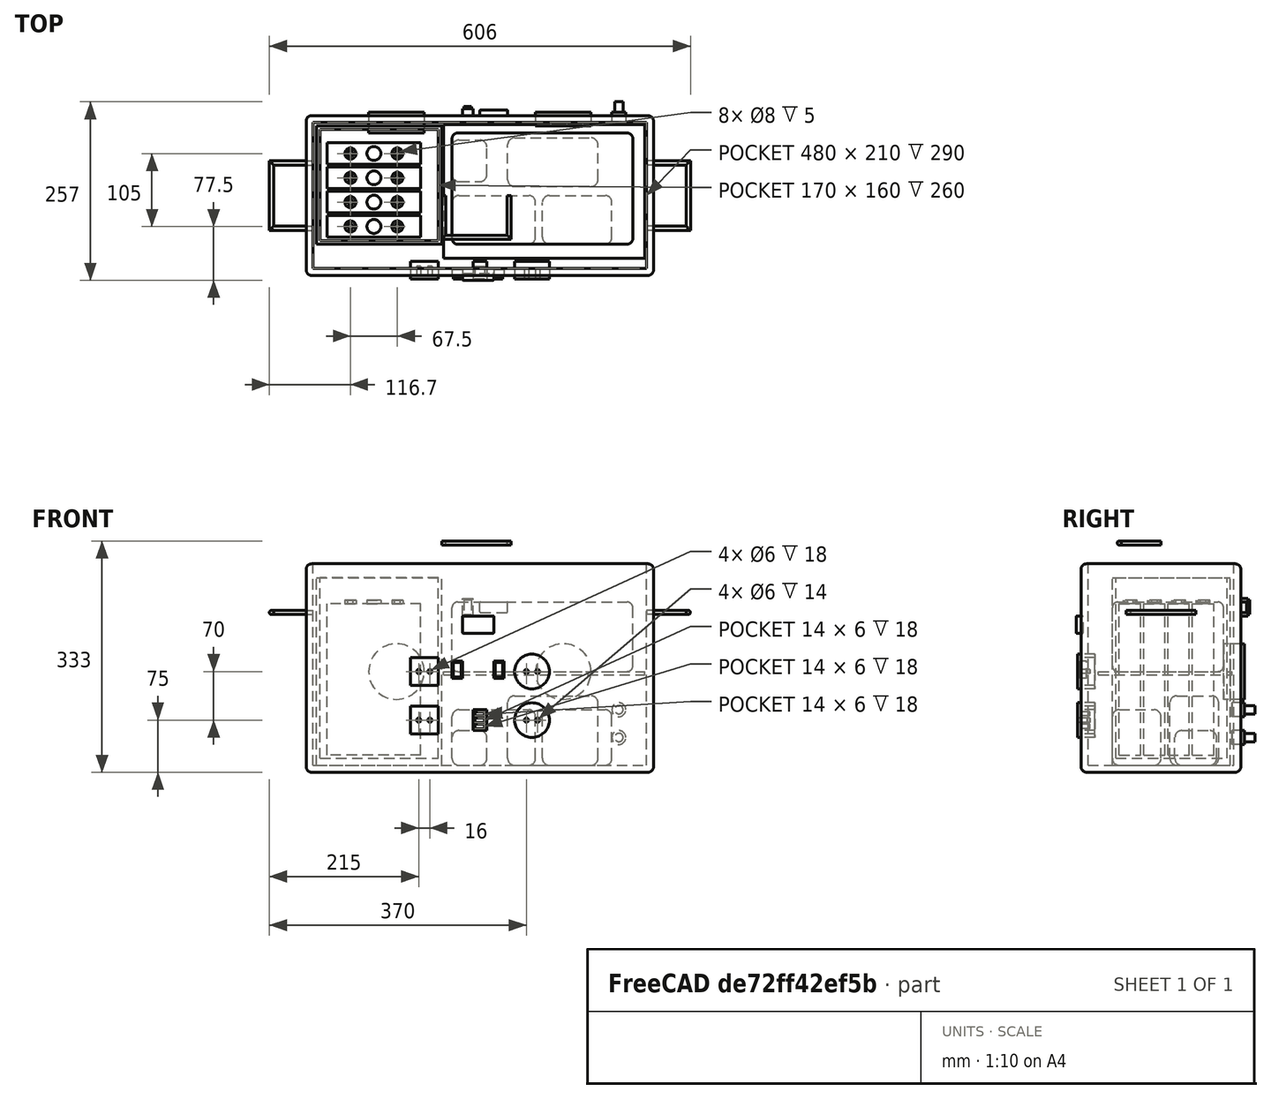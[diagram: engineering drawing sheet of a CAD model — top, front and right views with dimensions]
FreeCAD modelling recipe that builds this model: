
FCSTD DOCUMENT  (FreeCAD 0.16R6706 (Git))
Label: HOOU_FreeCAD_Solar_Box_v_02
License: All rights reserved
LicenseURL: http://en.wikipedia.org/wiki/All_rights_reserved
objects: Part::Box×26, Part::Cylinder×25, Part::Cut×14, Part::Fuse×11, Part::Fillet×9, Sketcher::SketchObject×4, PartDesign::Body×4, PartDesign::Pad×2, App::DocumentObjectGroup×1
note: 97 computed .brp shape members not serialized (recipe doc carries the construction recipe); baked Part::Feature solids carry a one-line shape summary decoded from their .brp

FEATURE [Part::Box] Box  label="Cube"
  Height = 300
  Length = 500
  Width = 230
FEATURE [Part::Box] Box001  label="Cube001"
  Height = 320
  Length = 480
  Placement = pos=(10,10,10) rot=(0,0,1;0rad)
  Width = 210
FEATURE [Part::Cut] Cut  label="Solar Box"
  Base = -> Box
  Tool = -> Box001
FEATURE [Sketcher::SketchObject] Sketch
FEATURE [Part::Box] Box002  label="Akku_box"
  Height = 290
  Length = 170
  Placement = pos=(20,50,20) rot=(0,0,1;0rad)
  Width = 160
FEATURE [Part::Box] Box003  label="MPPT"
  Height = 100
  Length = 130
  Placement = pos=(290,128,10) rot=(0,0,1;0rad)
  Width = 70
FEATURE [Part::Cylinder] Cylinder001  label="Fan 1"
  Angle = 360
  Height = 20
  Placement = pos=(370,235,145) rot=(1,0,0;1.5708rad)
  Radius = 40
FEATURE [PartDesign::Body] Body  label="AKKU 001"
  Placement = pos=(165,55,25) rot=(0,0,1;1.5708rad)
FEATURE [Sketcher::SketchObject] Sketch001
  sketch-geometry (4):
    g0: LineSegment StartX=0 StartY=135.1 StartZ=0 EndX=31 EndY=135.1 EndZ=0
    g1: LineSegment StartX=31 StartY=135.1 StartZ=0 EndX=31 EndY=0 EndZ=0
    g2: LineSegment StartX=31 StartY=0 StartZ=0 EndX=0 EndY=0 EndZ=0
    g3: LineSegment StartX=0 StartY=0 StartZ=0 EndX=0 EndY=135.1 EndZ=0
  constraints (11):
    c: Coincident(g0,g1)
    c: Coincident(g1,g2)
    c: Coincident(g2,g3)
    c: Coincident(g3,g0)
    c: Horizontal(g0)
    c: Horizontal(g2)
    c: Vertical(g1)
    c: Vertical(g3)
    c: Coincident(g2,g-1)
    c: DistanceY(g3,g3) = 135.1
    c: DistanceX(g2,g2) = 31
FEATURE [PartDesign::Pad] Pad
  Length = 217.3
  Length2 = 100
  Type = 0
FEATURE [Sketcher::SketchObject] Sketch002
  Placement = pos=(0,0,217.3) rot=(0,0,1;0rad)
  sketch-geometry (3):
    g0: Circle CenterX=15.5 CenterY=33.8 CenterZ=0 NormalX=0 NormalY=0 NormalZ=1 Radius=8
    g1: Circle CenterX=15.5 CenterY=67.55 CenterZ=0 NormalX=0 NormalY=0 NormalZ=1 Radius=10
    g2: Circle CenterX=15.5 CenterY=101.3 CenterZ=0 NormalX=0 NormalY=0 NormalZ=1 Radius=8
  constraints (9):
    c: DistanceY(g-1,g1) = 67.55
    c: DistanceX(g-1,g1) = 15.5
    c: DistanceX(g-1,g0) = 15.5
    c: DistanceX(g-1,g2) = 15.5
    c: DistanceY(g-1,g0) = 33.8
    c: DistanceY(g-1,g2) = 101.3
    c: Radius(g2) = 8
    c: Radius(g0) = 8
    c: Radius(g1) = 10
FEATURE [PartDesign::Pad] Pad001
  Length = 5.2
  Length2 = 100
  Type = 0
FEATURE [Sketcher::SketchObject] Sketch003
  Placement = pos=(0,0,222.5) rot=(0,0,1;0rad)
  sketch-geometry (2):
    g0: Circle CenterX=15.5 CenterY=101.3 CenterZ=0 NormalX=0 NormalY=0 NormalZ=1 Radius=4
    g1: Circle CenterX=15.5 CenterY=33.8 CenterZ=0 NormalX=0 NormalY=0 NormalZ=1 Radius=4
  constraints (6):
    c: Radius(g0) = 4
    c: DistanceY(g-1,g0) = 101.3
    c: DistanceX(g-1,g0) = 15.5
    c: Radius(g1) = 4
    c: DistanceX(g-1,g1) = 15.5
    c: DistanceY(g-1,g1) = 33.8
FEATURE [PartDesign::Body] Body001  label="AKKU 002"
  Placement = pos=(165,90,25) rot=(0,0,1;1.5708rad)
FEATURE [PartDesign::Body] Body002  label="AKKU 003"
  Placement = pos=(165,125,25) rot=(0,0,1;1.5708rad)
FEATURE [PartDesign::Body] Body003  label="AKKU 004"
  Placement = pos=(165,160,25) rot=(0,0,1;1.5708rad)
FEATURE [App::DocumentObjectGroup] Group  label="Akku"
  Group = -> [Body,XY_Plane,XZ_Plane,YZ_Plane,Sketch001,Pad,Sketch002,Pad001,Sketch003,Body001,Body002,Body003]
FEATURE [Part::Box] Box006  label="Akku_box001"
  Height = 270
  Length = 180
  Placement = pos=(15,45,10) rot=(0,0,1;0rad)
  Width = 170
FEATURE [Part::Cut] Cut003  label="Akku_pack"
  Base = -> Box006
  Tool = -> Box002
FEATURE [Part::Box] Box007  label="Switch Box"
  Height = 80
  Length = 100
  Placement = pos=(340,45,10) rot=(0,0,1;0rad)
  Width = 70
FEATURE [Part::Cylinder] Cylinder004  label="Fan 2"
  Angle = 360
  Height = 30
  Placement = pos=(130,235,145) rot=(1,0,0;1.5708rad)
  Radius = 40
FEATURE [Part::Box] Box008  label="Invertor"
  Height = 100
  Length = 260
  Placement = pos=(210,45,145) rot=(0,0,1;0rad)
  Width = 160
FEATURE [Part::Box] Box009  label="Fuse box"
  Height = 50
  Length = 50
  Placement = pos=(210,135,10) rot=(0,0,1;0rad)
  Width = 60
FEATURE [Part::Box] Box010  label="Box partation"
  Height = 5
  Length = 289
  Placement = pos=(198,25,140) rot=(0,0,1;0rad)
  Width = 192
FEATURE [Part::Cylinder] Cylinder  label="PV plug part 1"
  Angle = 360
  Height = 18
  Placement = pos=(450,235,50) rot=(1,0,0;1.5708rad)
  Radius = 10
FEATURE [Part::Cylinder] Cylinder006  label="PV plug part 2"
  Angle = 360
  Height = 15
  Placement = pos=(450,250,50) rot=(1,0,0;1.5708rad)
  Radius = 6
FEATURE [Part::Fuse] Fusion  label="PV Input Plug001"
  Base = -> Cylinder
  Tool = -> Cylinder006
FEATURE [Part::Cylinder] Cylinder007  label="PV plug part 003"
  Angle = 360
  Height = 18
  Placement = pos=(450,235,50) rot=(1,0,0;1.5708rad)
  Radius = 10
FEATURE [Part::Cylinder] Cylinder008  label="PV plug part 004"
  Angle = 360
  Height = 15
  Placement = pos=(450,250,50) rot=(1,0,0;1.5708rad)
  Radius = 6
FEATURE [Part::Fuse] Fusion002  label="PV Input Plug002"
  Base = -> Cylinder007
  Placement = pos=(0,0,40) rot=(0,0,1;0rad)
  Tool = -> Cylinder008
FEATURE [Part::Fillet] Fillet004  label="Solar Box      "
  Base = -> Cut
  Edges = 12 edges r=8: [Edge1,Edge2,Edge3,Edge4,Edge5,Edge6,Edge7,Edge8,Edge9,Edge14,Edge15,Edge16]
FEATURE [Part::Box] Box011  label="Temp. Disply"
  Height = 15
  Length = 40
  Placement = pos=(250,230,230) rot=(0,0,1;0rad)
  Width = 8
FEATURE [Part::Box] Box012  label="Fan Switch part 1"
  Height = 25
  Length = 15
  Placement = pos=(225,230,225) rot=(0,0,1;0rad)
  Width = 10
FEATURE [Part::Box] Box013  label="Fan Switch part 2"
  Height = 21
  Length = 11
  Placement = pos=(227,236,227) rot=(0,0,1;0rad)
  Width = 7
FEATURE [Part::Fuse] Fusion003  label="Fan Switch"
  Base = -> Box012
  Tool = -> Box013
FEATURE [Part::Fillet] Fillet  label="Temp. Disply "
  Base = -> Box011
  Edges = 12 edges r=1: [Edge1,Edge2,Edge3,Edge4,Edge5,Edge6,Edge7,Edge8,Edge9,Edge10,Edge11,Edge12]
FEATURE [Part::Box] Box014  label="BMS"
  Height = 80
  Length = 120
  Placement = pos=(210,45,10) rot=(0,0,1;0rad)
  Width = 70
FEATURE [Part::Box] Box015  label="Main Disply001"
  Height = 25
  Length = 45
  Placement = pos=(225,-7,200) rot=(0,0,1;0rad)
  Width = 10
FEATURE [Part::Fillet] Fillet005  label="Main Disply"
  Base = -> Box015
  Edges = 12 edges r=1: [Edge1,Edge2,Edge3,Edge4,Edge5,Edge6,Edge7,Edge8,Edge9,Edge10,Edge11,Edge12]
FEATURE [Part::Cylinder] Cylinder009  label="AC Plug part 1"
  Angle = 360
  Height = 25
  Placement = pos=(250,20,130) rot=(1,0,0;1.5708rad)
  Radius = 25
FEATURE [Part::Cylinder] Cylinder010  label="AC Plug part 2"
  Angle = 360
  Height = 15
  Placement = pos=(242,9,130) rot=(1,0,0;1.5708rad)
  Radius = 3
FEATURE [Part::Cylinder] Cylinder011  label="AC Plug part 3"
  Angle = 360
  Height = 15
  Placement = pos=(258,9,130) rot=(1,0,0;1.5708rad)
  Radius = 3
FEATURE [Part::Cut] Cut004
  Base = -> Cylinder009
  Tool = -> Cylinder010
FEATURE [Part::Cut] Cut005  label="AC Plug 1"
  Base = -> Cut004
  Placement = pos=(75,0,15) rot=(0,0,1;0rad)
  Tool = -> Cylinder011
FEATURE [Part::Cylinder] Cylinder012  label="AC Plug part 004"
  Angle = 360
  Height = 25
  Placement = pos=(250,20,130) rot=(1,0,0;1.5708rad)
  Radius = 25
FEATURE [Part::Cylinder] Cylinder013  label="AC Plug part 005"
  Angle = 360
  Height = 15
  Placement = pos=(242,9,130) rot=(1,0,0;1.5708rad)
  Radius = 3
FEATURE [Part::Cylinder] Cylinder014  label="AC Plug part 006"
  Angle = 360
  Height = 15
  Placement = pos=(258,9,130) rot=(1,0,0;1.5708rad)
  Radius = 3
FEATURE [Part::Cut] Cut006
  Base = -> Cylinder012
  Tool = -> Cylinder013
FEATURE [Part::Cut] Cut007  label="AC Plug 2"
  Base = -> Cut006
  Placement = pos=(75,0,-55) rot=(0,0,1;0rad)
  Tool = -> Cylinder014
FEATURE [Part::Box] Box016  label="DC Plug part 1"
  Height = 25
  Length = 40
  Placement = pos=(150,0,125) rot=(1,0,0;1.5708rad)
  Width = 40
FEATURE [Part::Cylinder] Cylinder015  label="DC Plug part 2"
  Angle = 360
  Height = 20
  Placement = pos=(178,-7,145) rot=(1,0,0;1.5708rad)
  Radius = 3
FEATURE [Part::Cylinder] Cylinder016  label="DC Plug part 3"
  Angle = 360
  Height = 20
  Placement = pos=(162,-7,145) rot=(1,0,0;1.5708rad)
  Radius = 3
FEATURE [Part::Cut] Cut008
  Base = -> Box016
  Tool = -> Cylinder015
FEATURE [Part::Cut] Cut009  label="DC Plug 1"
  Base = -> Cut008
  Placement = pos=(0,20,0) rot=(0,0,1;0rad)
  Tool = -> Cylinder016
FEATURE [Part::Box] Box017  label="DC Plug part 004"
  Height = 25
  Length = 40
  Placement = pos=(150,0,125) rot=(1,0,0;1.5708rad)
  Width = 40
FEATURE [Part::Cylinder] Cylinder017  label="DC Plug part 005"
  Angle = 360
  Height = 20
  Placement = pos=(178,-7,145) rot=(1,0,0;1.5708rad)
  Radius = 3
FEATURE [Part::Cylinder] Cylinder018  label="DC Plug part 006"
  Angle = 360
  Height = 20
  Placement = pos=(162,-7,145) rot=(1,0,0;1.5708rad)
  Radius = 3
FEATURE [Part::Cut] Cut010
  Base = -> Box017
  Tool = -> Cylinder017
FEATURE [Part::Cut] Cut011  label="DC Plug 2"
  Base = -> Cut010
  Placement = pos=(0,20,-70) rot=(0,0,1;0rad)
  Tool = -> Cylinder018
FEATURE [Part::Box] Box018  label="USB Plug"
  Height = 25
  Length = 20
  Placement = pos=(240,20,100) rot=(1,0,0;1.5708rad)
  Width = 30
FEATURE [Part::Box] Box019  label="USB Plug001"
  Height = 20
  Length = 14
  Placement = pos=(243,13,103) rot=(1,0,0;1.5708rad)
  Width = 6
FEATURE [Part::Box] Box020  label="USB Plug002"
  Height = 20
  Length = 14
  Placement = pos=(243,13,112) rot=(1,0,0;1.5708rad)
  Width = 6
FEATURE [Part::Box] Box021  label="USB Plug003"
  Height = 20
  Length = 14
  Placement = pos=(243,13,121) rot=(1,0,0;1.5708rad)
  Width = 6
FEATURE [Part::Cut] Cut012
  Base = -> Box018
  Tool = -> Box019
FEATURE [Part::Cut] Cut013
  Base = -> Cut012
  Tool = -> Box021
FEATURE [Part::Cut] Cut014  label="USB Plug  "
  Base = -> Cut013
  Placement = pos=(0,0,-40) rot=(0,0,1;0rad)
  Tool = -> Box020
FEATURE [Part::Box] Box022  label="Fan Switch part 003"
  Height = 25
  Length = 15
  Placement = pos=(225,230,225) rot=(0,0,1;0rad)
  Width = 10
FEATURE [Part::Box] Box023  label="Fan Switch part 004"
  Height = 21
  Length = 11
  Placement = pos=(227,236,227) rot=(0,0,1;0rad)
  Width = 7
FEATURE [Part::Fuse] Fusion004  label="DC Plug Switch"
  Base = -> Box022
  Placement = pos=(450,238,-90) rot=(0,0,1;3.14159rad)
  Tool = -> Box023
FEATURE [Part::Box] Box024  label="Fan Switch part 005"
  Height = 25
  Length = 15
  Placement = pos=(225,230,225) rot=(0,0,1;0rad)
  Width = 10
FEATURE [Part::Box] Box025  label="Fan Switch part 006"
  Height = 21
  Length = 11
  Placement = pos=(227,236,227) rot=(0,0,1;0rad)
  Width = 7
FEATURE [Part::Fuse] Fusion005  label="AC Plug Switch"
  Base = -> Box024
  Placement = pos=(510,238,-90) rot=(0,0,1;3.14159rad)
  Tool = -> Box025
FEATURE [Part::Fillet] Fillet006  label="Invertor  "
  Base = -> Box008
  Edges = 12 edges r=8: [Edge1,Edge2,Edge3,Edge4,Edge5,Edge6,Edge7,Edge8,Edge9,Edge10,Edge11,Edge12]
FEATURE [Part::Fillet] Fillet007  label="MPPT               "
  Base = -> Box003
  Edges = 12 edges r=10: [Edge1,Edge2,Edge3,Edge4,Edge5,Edge6,Edge7,Edge8,Edge9,Edge10,Edge11,Edge12]
FEATURE [Part::Fillet] Fillet008  label="switching Box"
  Base = -> Box007
  Edges = 12 edges r=10: [Edge1,Edge2,Edge3,Edge4,Edge5,Edge6,Edge7,Edge8,Edge9,Edge10,Edge11,Edge12]
FEATURE [Part::Fillet] Fillet009  label="Fuse Box"
  Base = -> Box009
  Edges = 12 edges r=10: [Edge1,Edge2,Edge3,Edge4,Edge5,Edge6,Edge7,Edge8,Edge9,Edge10,Edge11,Edge12]
FEATURE [Part::Fillet] Fillet010  label="BMS  "
  Base = -> Box014
  Edges = 12 edges r=10: [Edge1,Edge2,Edge3,Edge4,Edge5,Edge6,Edge7,Edge8,Edge9,Edge10,Edge11,Edge12]
FEATURE [Part::Cylinder] Cylinder019  label="Cylinder"
  Angle = 360
  Height = 100
  Placement = pos=(-50,0,0) rot=(1,0,0;1.5708rad)
  Radius = 3
FEATURE [Part::Cylinder] Cylinder020  label="Cylinder001"
  Angle = 360
  Height = 60
  Placement = pos=(-50,-3,0) rot=(0,1,0;1.5708rad)
  Radius = 3
FEATURE [Part::Cylinder] Cylinder021  label="Cylinder002"
  Angle = 360
  Height = 60
  Placement = pos=(-50,-97,0) rot=(0,1,0;1.5708rad)
  Radius = 3
FEATURE [Part::Fuse] Fusion006
  Base = -> Cylinder019
  Tool = -> Cylinder020
FEATURE [Part::Fuse] Fusion007  label="Handle Left"
  Base = -> Cylinder021
  Placement = pos=(0,165,230) rot=(0,0,1;0rad)
  Tool = -> Fusion006
FEATURE [Part::Cylinder] Cylinder022  label="Cylinder025"
  Angle = 360
  Height = 100
  Placement = pos=(-50,0,0) rot=(1,0,0;1.5708rad)
  Radius = 3
FEATURE [Part::Cylinder] Cylinder023  label="Cylinder026"
  Angle = 360
  Height = 60
  Placement = pos=(-50,-3,0) rot=(0,1,0;1.5708rad)
  Radius = 3
FEATURE [Part::Cylinder] Cylinder024  label="Cylinder027"
  Angle = 360
  Height = 60
  Placement = pos=(-50,-97,0) rot=(0,1,0;1.5708rad)
  Radius = 3
FEATURE [Part::Fuse] Fusion008
  Base = -> Cylinder022
  Tool = -> Cylinder023
FEATURE [Part::Fuse] Fusion009  label="Handle Right"
  Base = -> Cylinder024
  Placement = pos=(500,165,230) rot=(0,1,0;3.14159rad)
  Tool = -> Fusion008
FEATURE [Part::Box] Box026  label="Solar Box Top part 1"
  Height = 40
  Length = 520
  Placement = pos=(-10,-10,350) rot=(0,0,1;0rad)
  Width = 250
FEATURE [Part::Box] Box027  label="Solar Box Top part 2"
  Height = 30
  Length = 500
  Placement = pos=(0,0,350) rot=(0,0,1;0rad)
  Width = 230
FEATURE [Part::Cut] Cut015  label="Solar Box Top   "
  Base = -> Box026
  Tool = -> Box027
FEATURE [Part::Fillet] Fillet011  label="Solar Box Top"
  Base = -> Cut015
  Edges = 24 edges r=8: [Edge1,Edge2,Edge3,Edge4,Edge5,Edge6,Edge7,Edge8,Edge9,Edge10,Edge11,Edge12,Edge13,Edge14,Edge15,Edge16,Edge17,Edge18,Edge19,Edge20,Edge21,Edge22,Edge23,Edge24]
  Placement = pos=(0,0,-60) rot=(0,0,1;0rad)
FEATURE [Part::Cylinder] Cylinder025  label="Cylinder031"
  Angle = 360
  Height = 100
  Placement = pos=(-50,0,0) rot=(1,0,0;1.5708rad)
  Radius = 3
FEATURE [Part::Cylinder] Cylinder026  label="Cylinder032"
  Angle = 360
  Height = 60
  Placement = pos=(-50,-3,0) rot=(0,1,0;1.5708rad)
  Radius = 3
FEATURE [Part::Cylinder] Cylinder027  label="Cylinder033"
  Angle = 360
  Height = 60
  Placement = pos=(-50,-97,0) rot=(0,1,0;1.5708rad)
  Radius = 3
FEATURE [Part::Fuse] Fusion010
  Base = -> Cylinder025
  Tool = -> Cylinder026
FEATURE [Part::Fuse] Fusion011  label="Handle Top"
  Base = -> Cylinder027
  Placement = pos=(195,105,330) rot=(0,0,1;1.5708rad)
  Tool = -> Fusion010
